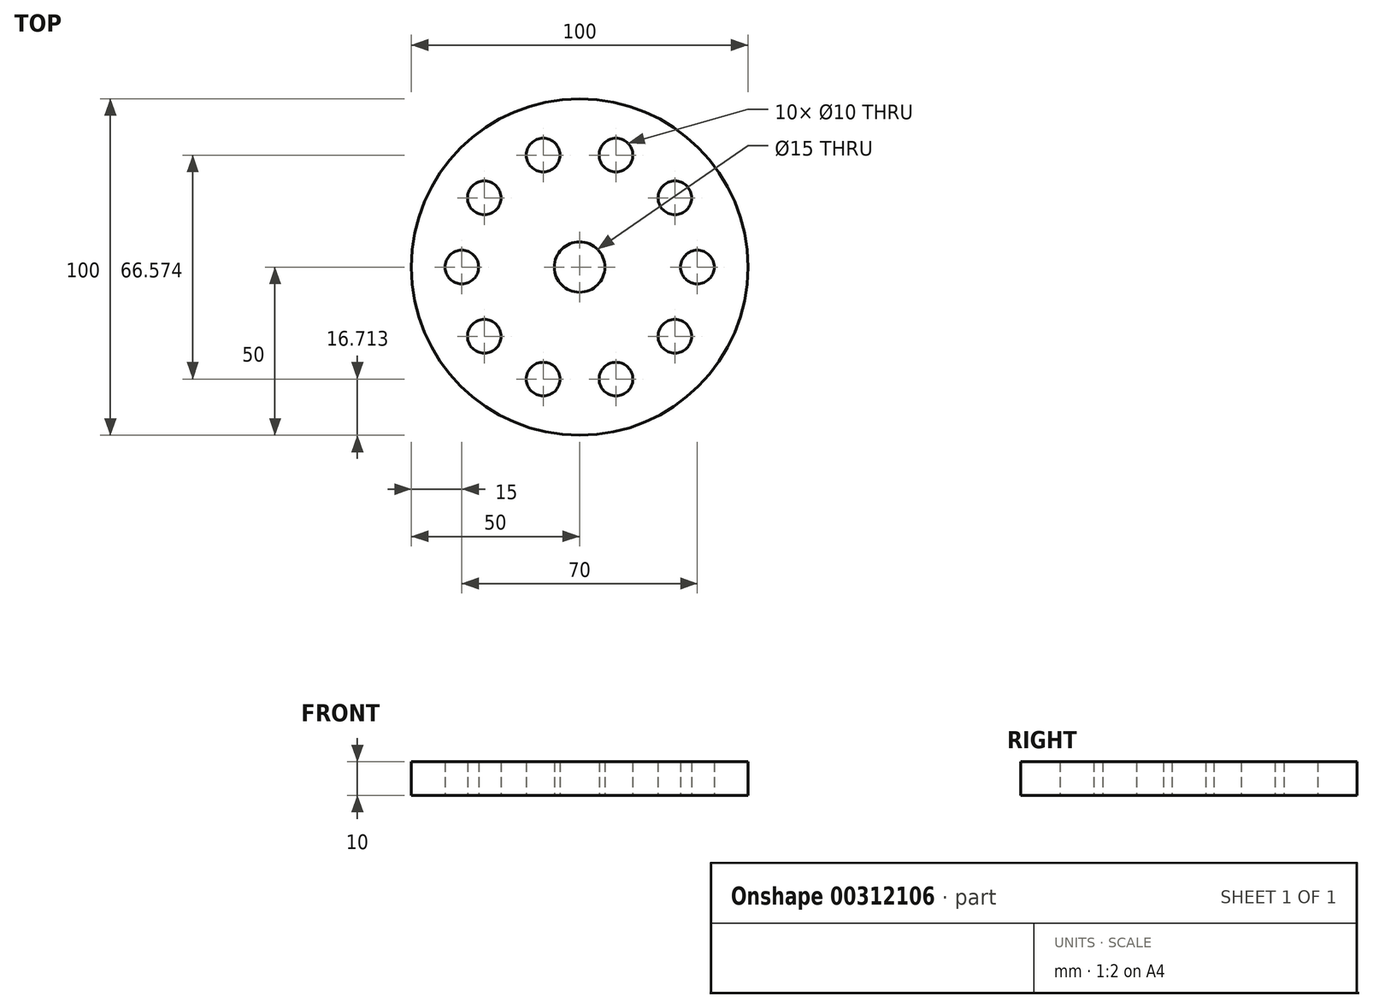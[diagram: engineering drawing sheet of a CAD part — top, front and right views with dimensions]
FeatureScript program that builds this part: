
annotation { "Feature Type Name" : "Feature", "Feature Type Description" : "" }
export const myFeature = defineFeature(function(context is Context, id is Id, definition is map)
    precondition{}
    {
        {
            var Q0;
            Q0=qCreatedBy(makeId("Top.planeOp"),FACE);
            var sketch = newSketch(context, id + "F0", { "sketchPlane" : qUnion([Q0])});
            skCircle(sketch, "E0", {"center": v(0, 0) * mm, "radius": 50 * mm});
            skLineSegment(sketch, "E1", {"start": v(0, 0) * mm, "end": v(35, 0) * mm, "construction": true});
            skCircle(sketch, "E2", {"center": v(35, 0) * mm, "radius": 5 * mm});
            skCircle(sketch, "E3.1.0", {"center": v(28.32, 20.57) * mm, "radius": 5 * mm});
            skCircle(sketch, "E3.2.0", {"center": v(10.82, 33.29) * mm, "radius": 5 * mm});
            skCircle(sketch, "E3.3.0", {"center": v(-10.82, 33.29) * mm, "radius": 5 * mm});
            skCircle(sketch, "E3.4.0", {"center": v(-28.32, 20.57) * mm, "radius": 5 * mm});
            skCircle(sketch, "E3.5.0", {"center": v(-35, 0) * mm, "radius": 5 * mm});
            skCircle(sketch, "E3.6.0", {"center": v(-28.32, -20.57) * mm, "radius": 5 * mm});
            skCircle(sketch, "E3.7.0", {"center": v(-10.82, -33.29) * mm, "radius": 5 * mm});
            skCircle(sketch, "E3.8.0", {"center": v(10.82, -33.29) * mm, "radius": 5 * mm});
            skCircle(sketch, "E3.9.0", {"center": v(28.32, -20.57) * mm, "radius": 5 * mm});
            skCircle(sketch, "E4", {"center": v(0, 0) * mm, "radius": 7.5 * mm});
            skSolve(sketch);
        }
        {
            var Q0;
            Q0=makeQuery(id+"F0.imprint","IMPRINT",FACE,{"disambiguationData":[TD([[makeQuery(id+"F0.imprint","IMPRINT",EDGE,{"derivedFrom":sQuery(id+"F0.wireOp",EDGE,"E0")}),1.0]])]});
            extrude(context, id + "F1", {"entities" : qUnion([Q0]), "depth" : 10 * mm});
        }
    });
